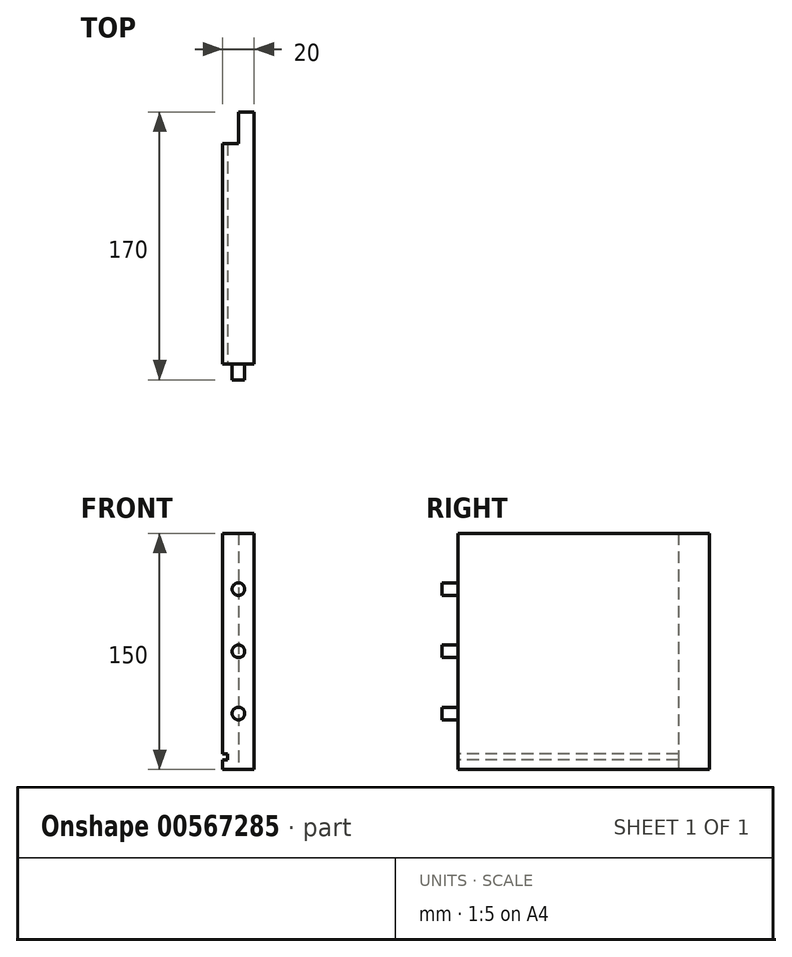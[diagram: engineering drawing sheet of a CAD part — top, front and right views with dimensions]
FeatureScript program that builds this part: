
annotation { "Feature Type Name" : "Feature", "Feature Type Description" : "" }
export const myFeature = defineFeature(function(context is Context, id is Id, definition is map)
    precondition{}
    {
        {
            var Q0;
            Q0=qCreatedBy(makeId("Right.planeOp"),FACE);
            var sketch = newSketch(context, id + "F0", { "sketchPlane" : qUnion([Q0])});
            skLineSegment(sketch, "E0.bottom", {"start": v(-124.65, 107.57) * mm, "end": v(55.35, 107.57) * mm});
            skLineSegment(sketch, "E0.top", {"start": v(-124.65, -42.43) * mm, "end": v(55.35, -42.43) * mm});
            skLineSegment(sketch, "E0.left", {"start": v(-124.65, 107.57) * mm, "end": v(-124.65, -42.43) * mm});
            skLineSegment(sketch, "E0.right", {"start": v(55.35, 107.57) * mm, "end": v(55.35, -42.43) * mm});
            skLineSegment(sketch, "E1", {"start": v(-104.65, 107.57) * mm, "end": v(-104.65, -42.43) * mm});
            skSolve(sketch);
        }
        {
            var Q0;
            {var subQ0=sQuery(id+"F0.wireOp",EDGE,"E0.right");Q0=makeQuery(id+"F0.imprint","IMPRINT",FACE,{"disambiguationData":[TD([[makeQuery(id+"F0.imprint","IMPRINT",EDGE,{"derivedFrom":subQ0}),-1.0]])]});}
            extrude(context, id + "F1", {"entities" : qUnion([Q0]), "depth" : 20 * mm, "offsetDistance" : 25 * mm});
        }
        {
            var Q0;
            Q0=makeQuery(id+"F1.opExtrude","CAP_FACE",FACE,{"disambiguationData":[OSD([sQuery(id+"F0.wireOp",EDGE,"E0.bottom"),sQuery(id+"F0.wireOp",EDGE,"E0.top"),sQuery(id+"F0.wireOp",EDGE,"E0.right"),sQuery(id+"F0.wireOp",EDGE,"E1")])],"isStart":true});
            var sketch = newSketch(context, id + "F2", { "sketchPlane" : qUnion([Q0])});
            skLineSegment(sketch, "E2", {"start": v(-35.35, 107.57) * mm, "end": v(-35.35, -42.43) * mm});
            skSolve(sketch);
        }
        {
            var Q0;
            {var subQ0=sQuery(id+"F2.wireOp",EDGE,"E2");Q0=makeQuery(id+"F2.imprint","IMPRINT",FACE,{"disambiguationData":[TD([[makeQuery(id+"F2.imprint","IMPRINT",EDGE,{"derivedFrom":subQ0}),-1.0]])]});}
            extrude(context, id + "F3", {"entities" : qUnion([Q0]), "operationType" : NewBodyOperationType.REMOVE, "oppositeDirection" : true, "depth" : 10 * mm, "offsetDistance" : 25 * mm});
        }
        {
            var Q0;
            Q0=makeQuery(id+"F1.opExtrude","SWEPT_FACE",FACE,{"disambiguationData":[OSD([sQuery(id+"F0.wireOp",EDGE,"E1")])]});
            var sketch = newSketch(context, id + "F4", { "sketchPlane" : qUnion([Q0])});
            skCircle(sketch, "E3", {"center": v(10, -6.93) * mm, "radius": 4 * mm});
            skCircle(sketch, "E4", {"center": v(10, 32.57) * mm, "radius": 4 * mm});
            skCircle(sketch, "E5", {"center": v(10, 72.07) * mm, "radius": 4 * mm});
            skSolve(sketch);
        }
        {
            var Q0;
            Q0=makeQuery(id+"F1.opExtrude","CAP_FACE",FACE,{"disambiguationData":[OSD([sQuery(id+"F0.wireOp",EDGE,"E0.bottom"),sQuery(id+"F0.wireOp",EDGE,"E0.top"),sQuery(id+"F0.wireOp",EDGE,"E0.right"),sQuery(id+"F0.wireOp",EDGE,"E1")])],"isStart":true});
            var sketch = newSketch(context, id + "F5", { "sketchPlane" : qUnion([Q0])});
            skLineSegment(sketch, "E6", {"start": v(-35.35, -32.43) * mm, "end": v(104.65, -32.43) * mm});
            skLineSegment(sketch, "E7", {"start": v(-35.35, -36.43) * mm, "end": v(104.65, -36.43) * mm});
            skSolve(sketch);
        }
        {
            var Q0;
            {var subQ0=sQuery(id+"F5.wireOp",EDGE,"E6");Q0=makeQuery(id+"F5.imprint","IMPRINT",FACE,{"disambiguationData":[TD([[makeQuery(id+"F5.imprint","IMPRINT",EDGE,{"derivedFrom":subQ0}),-1.0]])]});}
            extrude(context, id + "F6", {"entities" : qUnion([Q0]), "operationType" : NewBodyOperationType.REMOVE, "oppositeDirection" : true, "depth" : 3 * mm, "offsetDistance" : 25 * mm});
        }
        {
            var Q0;
            Q0=makeQuery(id+"F4.imprint","IMPRINT",FACE,{"disambiguationData":[TD([[makeQuery(id+"F4.imprint","IMPRINT",EDGE,{"derivedFrom":sQuery(id+"F4.wireOp",EDGE,"E5")}),1.0]])]});
            var Q1;
            Q1=makeQuery(id+"F4.imprint","IMPRINT",FACE,{"disambiguationData":[TD([[makeQuery(id+"F4.imprint","IMPRINT",EDGE,{"derivedFrom":sQuery(id+"F4.wireOp",EDGE,"E4")}),1.0]])]});
            var Q2;
            Q2=makeQuery(id+"F4.imprint","IMPRINT",FACE,{"disambiguationData":[TD([[makeQuery(id+"F4.imprint","IMPRINT",EDGE,{"derivedFrom":sQuery(id+"F4.wireOp",EDGE,"E3")}),1.0]])]});
            extrude(context, id + "F7", {"entities" : qUnion([Q0, Q1, Q2]), "operationType" : NewBodyOperationType.ADD, "depth" : 10 * mm, "offsetDistance" : 25 * mm});
        }
    });
